# Revit family: Dock-Seal_Perma-Tech_FIREguard-F-Curtain
name_source: partatom
category: Generic Models
units: mm (PartAtom-declared; Revit-internal decimal feet)

## family parameters
Always vertical = Yes
Can host rebar = No
Cut with Voids When Loaded = Yes
Host = Wall
Maintain Annotation Orientation = No
Part Type = Normal
Room Calculation Point = No
Round Connector Dimension = Use Diameter
Shared = No

## types (1)
- FIREguard F-Curtain
    Arcat Spec = https://www.arcat.com
    Cost = 0 $
    Cover = Cover Black
    Curtain Drop = 23"
    Curtain Length = 67"
    Default Elevation = 0"
    Manufacturer = Perma Tech Inc.
    Model = Perma FIREguard Dock Seal
    Opening Height = 84"
    Opening Width = 51"
    Outside Proj. = 11 1/2"
    Product Documentation Link = https://www.permatechinc.com
    Product Info = https://www.arcat.com
    Product Page URL = https://www.permatechinc.com
    Proj. At Bottom = 12"
    Proj. At Top = 12"
    Specification = https://www.permatechinc.com
    URL = https://www.permatechinc.com
    Unit Height = 90"
    Unit Width = 55"
    Width At Face = 12"
    Width At Rear = 7"

## geometry (parser evidence)
native form markers: Sweep x4
no freeform markers — native parametric forms only
